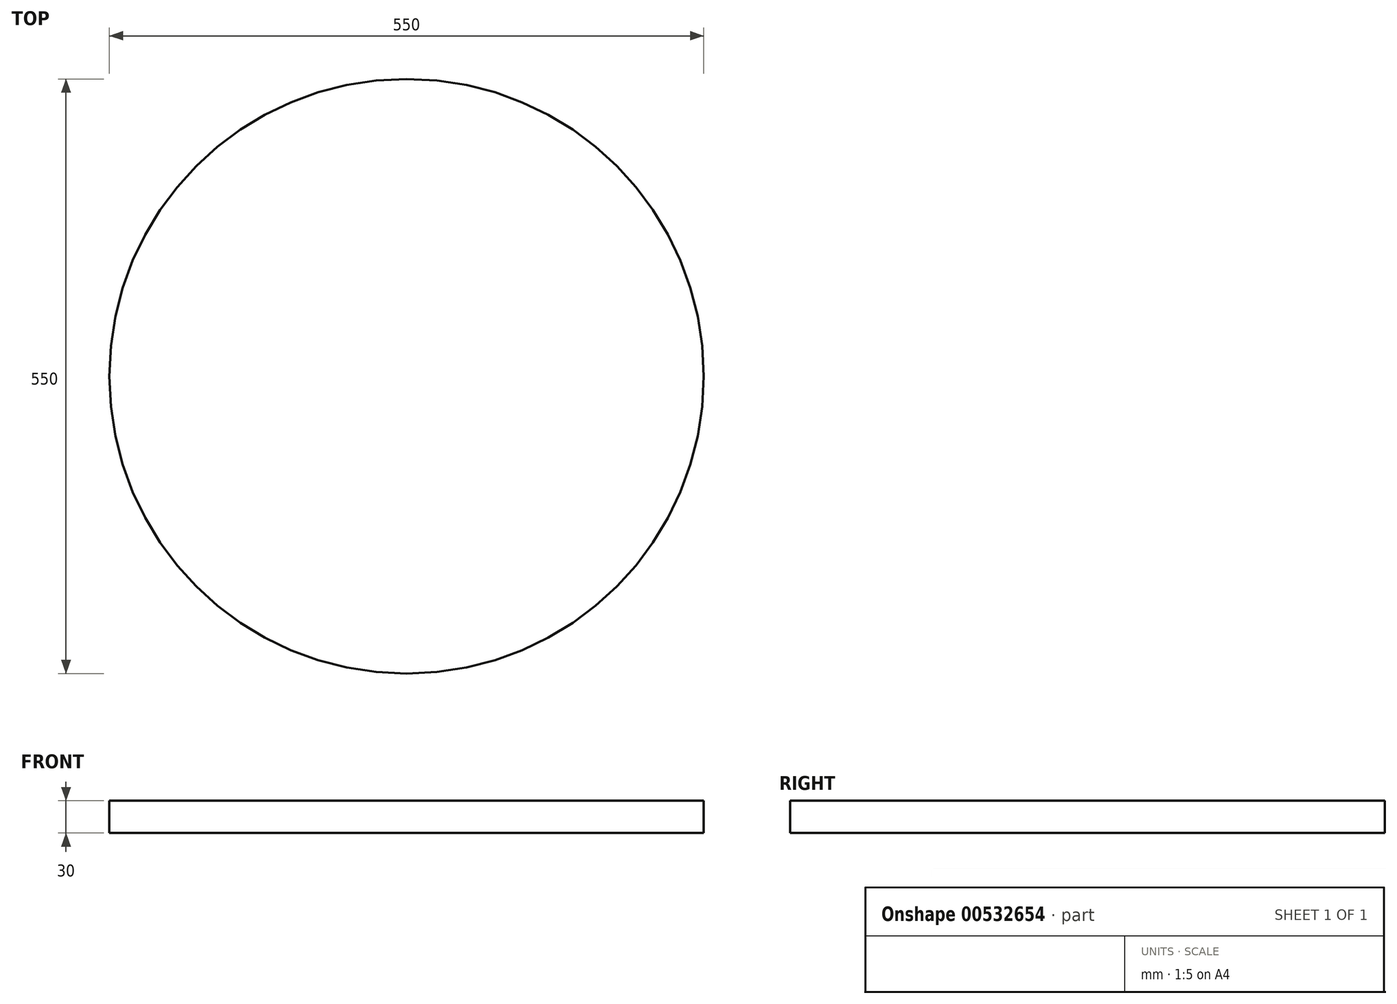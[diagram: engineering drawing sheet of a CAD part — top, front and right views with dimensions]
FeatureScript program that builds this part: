
annotation { "Feature Type Name" : "Feature", "Feature Type Description" : "" }
export const myFeature = defineFeature(function(context is Context, id is Id, definition is map)
    precondition{}
    {
        {
            var Q0;
            Q0=qCreatedBy(makeId("Top.planeOp"),FACE);
            var sketch = newSketch(context, id + "F0", { "sketchPlane" : qUnion([Q0])});
            skCircle(sketch, "E0", {"center": v(0, 0) * mm, "radius": 275 * mm});
            skSolve(sketch);
        }
        {
            var Q0;
            Q0 = qSketchRegion(id + "F0", true);
            extrude(context, id + "F1", {"entities" : qUnion([Q0]), "depth" : 30 * mm, "offsetDistance" : 25 * mm});
        }
    });
